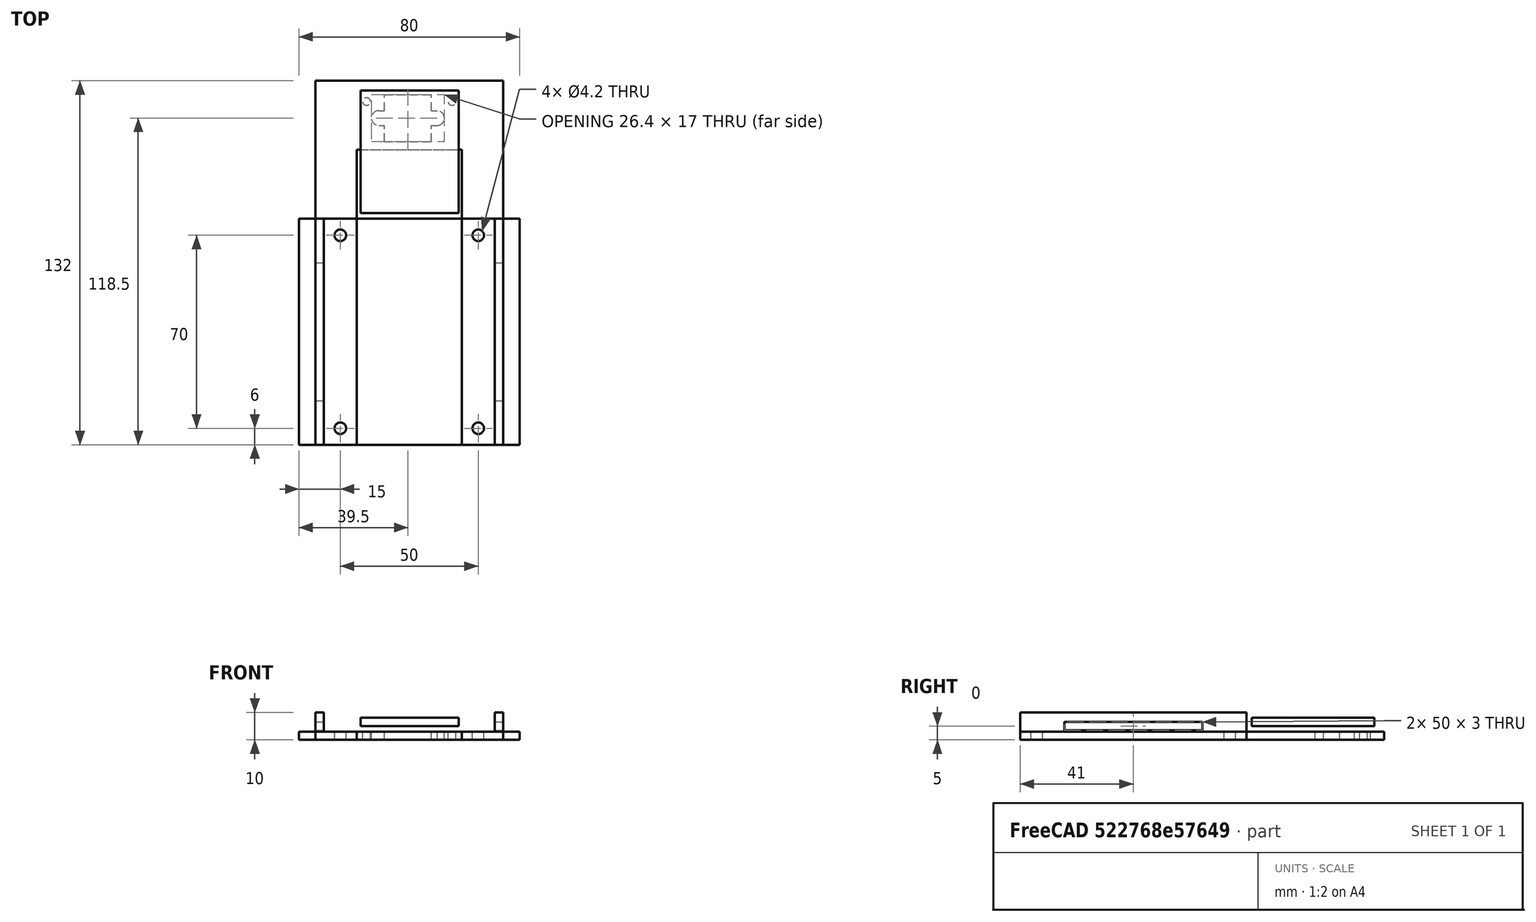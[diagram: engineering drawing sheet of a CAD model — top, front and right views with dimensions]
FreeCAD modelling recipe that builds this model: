
FCSTD DOCUMENT  (FreeCAD 0.15R4671 (Git))
Label: Enclosure_supports_OpenMV
License: All rights reserved
LicenseURL: http://en.wikipedia.org/wiki/All_rights_reserved
objects: Part::Box×14, Part::Cylinder×8, Part::MultiFuse×6, Part::Cut×5
note: 33 computed .brp shape members not serialized (recipe doc carries the construction recipe); baked Part::Feature solids carry a one-line shape summary decoded from their .brp

FEATURE [Part::Box] Box  label="base1"
  Height = 3
  Length = 15
  Width = 82
FEATURE [Part::Box] Box001  label="side1"
  Height = 10
  Length = 3
  Width = 82
FEATURE [Part::Box] Box002  label="base2"
  Height = 3
  Length = 15
  Placement = pos=(53,0,0) rot=(0,0,1;0rad)
  Width = 82
FEATURE [Part::Box] Box003  label="side2"
  Height = 10
  Length = 3
  Placement = pos=(65,0,0) rot=(0,0,1;0rad)
  Width = 82
FEATURE [Part::Cylinder] Cylinder  label="hole1"
  Angle = 360
  Height = 3
  Placement = pos=(9,76,0) rot=(0,0,1;0rad)
  Radius = 2.1
FEATURE [Part::Cylinder] Cylinder001  label="hole2"
  Angle = 360
  Height = 3
  Placement = pos=(59,76,0) rot=(0,0,1;0rad)
  Radius = 2.1
FEATURE [Part::Cylinder] Cylinder002  label="hole3"
  Angle = 360
  Height = 3
  Placement = pos=(9,6,0) rot=(0,0,1;0rad)
  Radius = 2.1
FEATURE [Part::Cylinder] Cylinder003  label="hole4"
  Angle = 360
  Height = 3
  Placement = pos=(59,6,0) rot=(0,0,1;0rad)
  Radius = 2.1
FEATURE [Part::MultiFuse] Fusion
  Shapes = -> [Cylinder,Cylinder002]
FEATURE [Part::MultiFuse] Fusion001
  Shapes = -> [Cylinder003,Cylinder001]
FEATURE [Part::Cut] Cut
  Base = -> Box
  Tool = -> Fusion
FEATURE [Part::Cut] Cut001
  Base = -> Box002
  Tool = -> Fusion001
FEATURE [Part::Box] Box004  label="side1_cut"
  Height = 3
  Length = 3
  Placement = pos=(0,16,3.5) rot=(0,0,1;0rad)
  Width = 50
FEATURE [Part::Box] Box005  label="side2_cut"
  Height = 3
  Length = 3
  Placement = pos=(65,16,3.5) rot=(0,0,1;0rad)
  Width = 50
FEATURE [Part::Cut] Cut002
  Base = -> Box001
  Tool = -> Box004
FEATURE [Part::Cut] Cut003
  Base = -> Box003
  Tool = -> Box005
FEATURE [Part::Box] Box006  label="G366"
  Height = 3
  Length = 80
  Placement = pos=(-6,0,0) rot=(0,0,1;0rad)
  Width = 82
FEATURE [Part::Box] Box007  label="OpenMV1"
  Height = 3
  Length = 15
  Placement = pos=(0,82,0) rot=(0,0,1;0rad)
  Width = 50
FEATURE [Part::Box] Box008  label="Cam"
  Height = 3
  Length = 35.56
  Placement = pos=(16.3,84,5) rot=(0,0,1;0rad)
  Width = 44.45
FEATURE [Part::Box] Box009  label="OpenMV1_2"
  Height = 3
  Length = 38
  Placement = pos=(15,107,0) rot=(0,0,1;0rad)
  Width = 25
FEATURE [Part::Box] Box010  label="OpenMV2"
  Height = 3
  Length = 15
  Placement = pos=(53,82,0) rot=(0,0,1;0rad)
  Width = 50
FEATURE [Part::Box] Box011  label="OpenMV_2_cut001"
  Height = 3
  Length = 17
  Placement = pos=(25,110,0) rot=(0,0,1;0rad)
  Width = 17
FEATURE [Part::Cylinder] Cylinder004  label="OpenMV_2_cut"
  Angle = 360
  Height = 3
  Placement = pos=(23,118.5,0) rot=(0,0,1;0rad)
  Radius = 2.7
FEATURE [Part::Cylinder] Cylinder005  label="OpenMV_2_cut002"
  Angle = 360
  Height = 3
  Placement = pos=(44,118.5,0) rot=(0,0,1;0rad)
  Radius = 2.7
FEATURE [Part::MultiFuse] Fusion003
  Shapes = -> [Box010,Box007,Box009]
FEATURE [Part::Cylinder] Cylinder006  label="Hole1"
  Angle = 360
  Height = 3
  Placement = pos=(18.508,124.5,0) rot=(0,0,1;0rad)
  Radius = 1.397
FEATURE [Part::Cylinder] Cylinder007  label="Hole2"
  Angle = 360
  Height = 3
  Placement = pos=(49.508,124.5,0) rot=(0,0,1;0rad)
  Radius = 1.397
FEATURE [Part::MultiFuse] Fusion005
  Shapes = -> [Cut001,Cut003]
FEATURE [Part::MultiFuse] Fusion006
  Shapes = -> [Cut002,Cut]
FEATURE [Part::Box] Box012  label="OpenMV_2_cut003"
  Height = 3
  Length = 5.2
  Placement = pos=(23,115.8,0) rot=(0,0,1;0rad)
  Width = 5.4
FEATURE [Part::Box] Box013  label="OpenMV_2_cut004"
  Height = 3
  Length = 5.2
  Placement = pos=(39,115.8,0) rot=(0,0,1;0rad)
  Width = 5.4
FEATURE [Part::MultiFuse] Fusion007
  Shapes = -> [Box013,Cylinder007,Cylinder006,Box011,Cylinder004,Cylinder005,Box012]
FEATURE [Part::Cut] Cut004
  Base = -> Fusion003
  Tool = -> Fusion007
